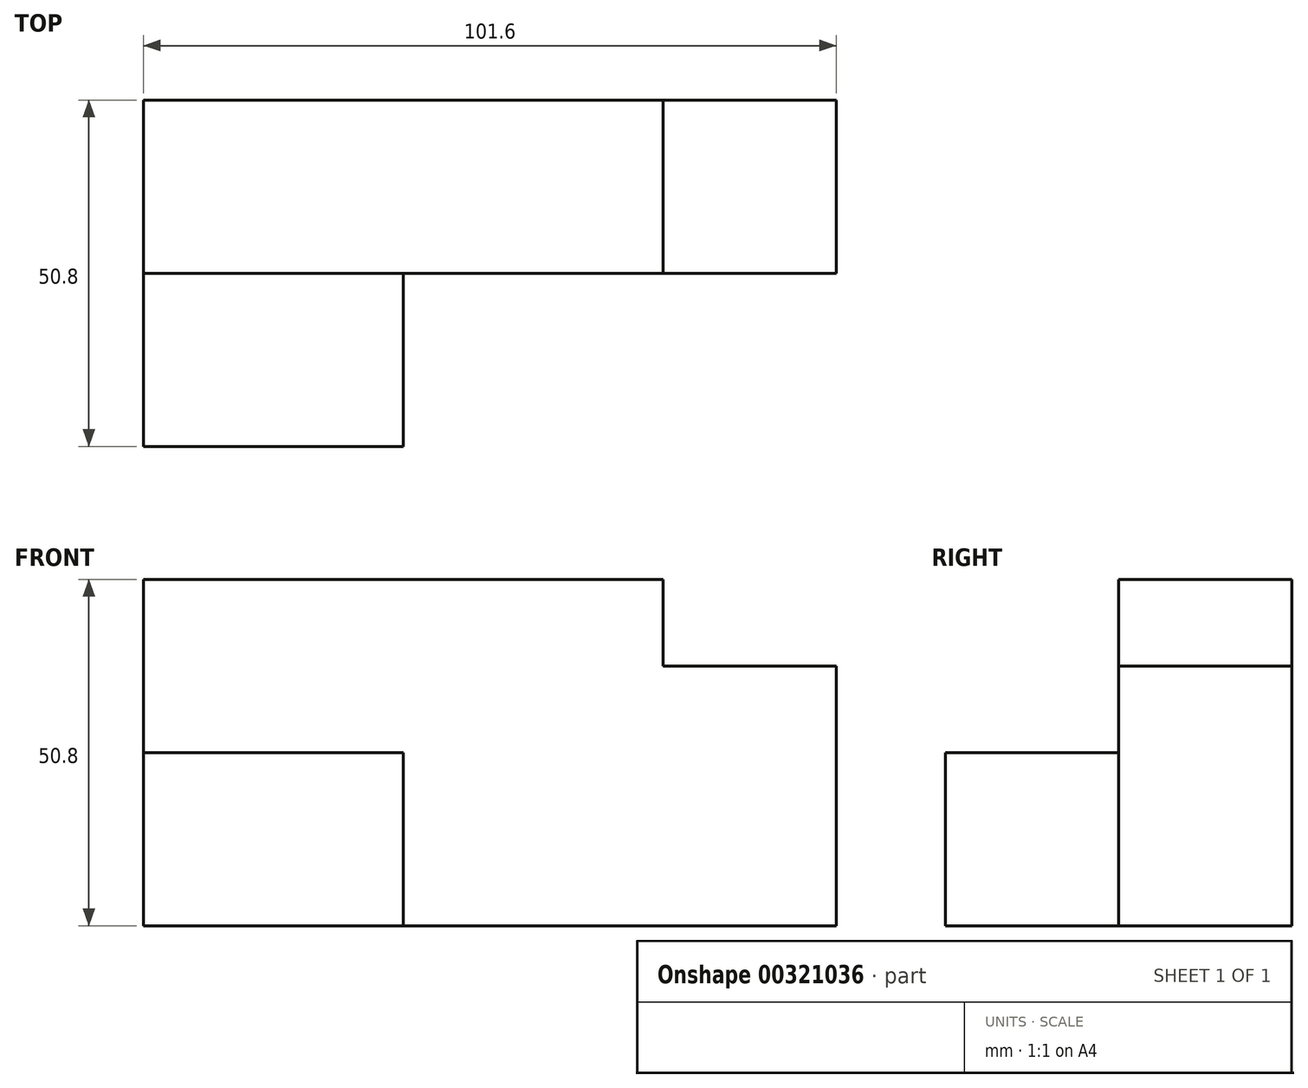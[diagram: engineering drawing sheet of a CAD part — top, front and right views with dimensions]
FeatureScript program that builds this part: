
annotation { "Feature Type Name" : "Feature", "Feature Type Description" : "" }
export const myFeature = defineFeature(function(context is Context, id is Id, definition is map)
    precondition{}
    {
        {
            var Q0;
            Q0=qCreatedBy(makeId("Right.planeOp"),FACE);
            var sketch = newSketch(context, id + "F0", { "sketchPlane" : qUnion([Q0])});
            skLineSegment(sketch, "E0.bottom", {"start": v(-39.16, 28.5) * mm, "end": v(-13.76, 28.5) * mm});
            skLineSegment(sketch, "E0.top", {"start": v(-39.16, -22.3) * mm, "end": v(-13.76, -22.3) * mm});
            skLineSegment(sketch, "E0.left", {"start": v(-39.16, 28.5) * mm, "end": v(-39.16, -22.3) * mm});
            skLineSegment(sketch, "E0.right", {"start": v(-13.76, 28.5) * mm, "end": v(-13.76, -22.3) * mm});
            skSolve(sketch);
        }
        {
            var Q0;
            Q0=makeQuery(id+"F0.imprint","IMPRINT",FACE,{"disambiguationData":[TD([[makeQuery(id+"F0.imprint","IMPRINT",EDGE,{"derivedFrom":sQuery(id+"F0.wireOp",EDGE,"E0.bottom")}),-1.0]])]});
            extrude(context, id + "F1", {"entities" : qUnion([Q0]), "depth" : 101.6 * mm});
        }
        {
            var Q0;
            Q0=makeQuery(id+"F1.opExtrude","SWEPT_FACE",FACE,{"disambiguationData":[OSD([sQuery(id+"F0.wireOp",EDGE,"E0.bottom")])]});
            var sketch = newSketch(context, id + "F2", { "sketchPlane" : qUnion([Q0])});
            skLineSegment(sketch, "E1", {"start": v(101.6, -13.76) * mm, "end": v(76.2, -13.76) * mm});
            skLineSegment(sketch, "E2", {"start": v(76.2, -13.76) * mm, "end": v(76.2, -39.16) * mm});
            skLineSegment(sketch, "E3", {"start": v(76.2, -39.16) * mm, "end": v(101.6, -39.16) * mm});
            skLineSegment(sketch, "E4", {"start": v(101.6, -39.16) * mm, "end": v(101.6, -13.76) * mm});
            skSolve(sketch);
        }
        {
            var Q0;
            Q0=makeQuery(id+"F2.imprint","IMPRINT",FACE,{"disambiguationData":[TD([[makeQuery(id+"F2.imprint","IMPRINT",EDGE,{"derivedFrom":sQuery(id+"F2.wireOp",EDGE,"E1")}),1.0]])]});
            extrude(context, id + "F3", {"entities" : qUnion([Q0]), "operationType" : NewBodyOperationType.REMOVE, "oppositeDirection" : true, "depth" : 12.7 * mm});
        }
        {
            var Q0;
            Q0=makeQuery(id+"F1.opExtrude","SWEPT_FACE",FACE,{"disambiguationData":[OSD([sQuery(id+"F0.wireOp",EDGE,"E0.left")])]});
            var sketch = newSketch(context, id + "F4", { "sketchPlane" : qUnion([Q0])});
            skLineSegment(sketch, "E5.bottom", {"start": v(0, -22.3) * mm, "end": v(38.1, -22.3) * mm});
            skLineSegment(sketch, "E5.top", {"start": v(0, 3.1) * mm, "end": v(38.1, 3.1) * mm});
            skLineSegment(sketch, "E5.left", {"start": v(0, -22.3) * mm, "end": v(0, 3.1) * mm});
            skLineSegment(sketch, "E5.right", {"start": v(38.1, -22.3) * mm, "end": v(38.1, 3.1) * mm});
            skSolve(sketch);
        }
        {
            var Q0;
            Q0=makeQuery(id+"F4.imprint","IMPRINT",FACE,{"disambiguationData":[TD([[makeQuery(id+"F4.imprint","IMPRINT",EDGE,{"derivedFrom":sQuery(id+"F4.wireOp",EDGE,"E5.bottom")}),-1.0]])]});
            extrude(context, id + "F5", {"entities" : qUnion([Q0]), "operationType" : NewBodyOperationType.ADD, "depth" : 25.4 * mm});
        }
    });
